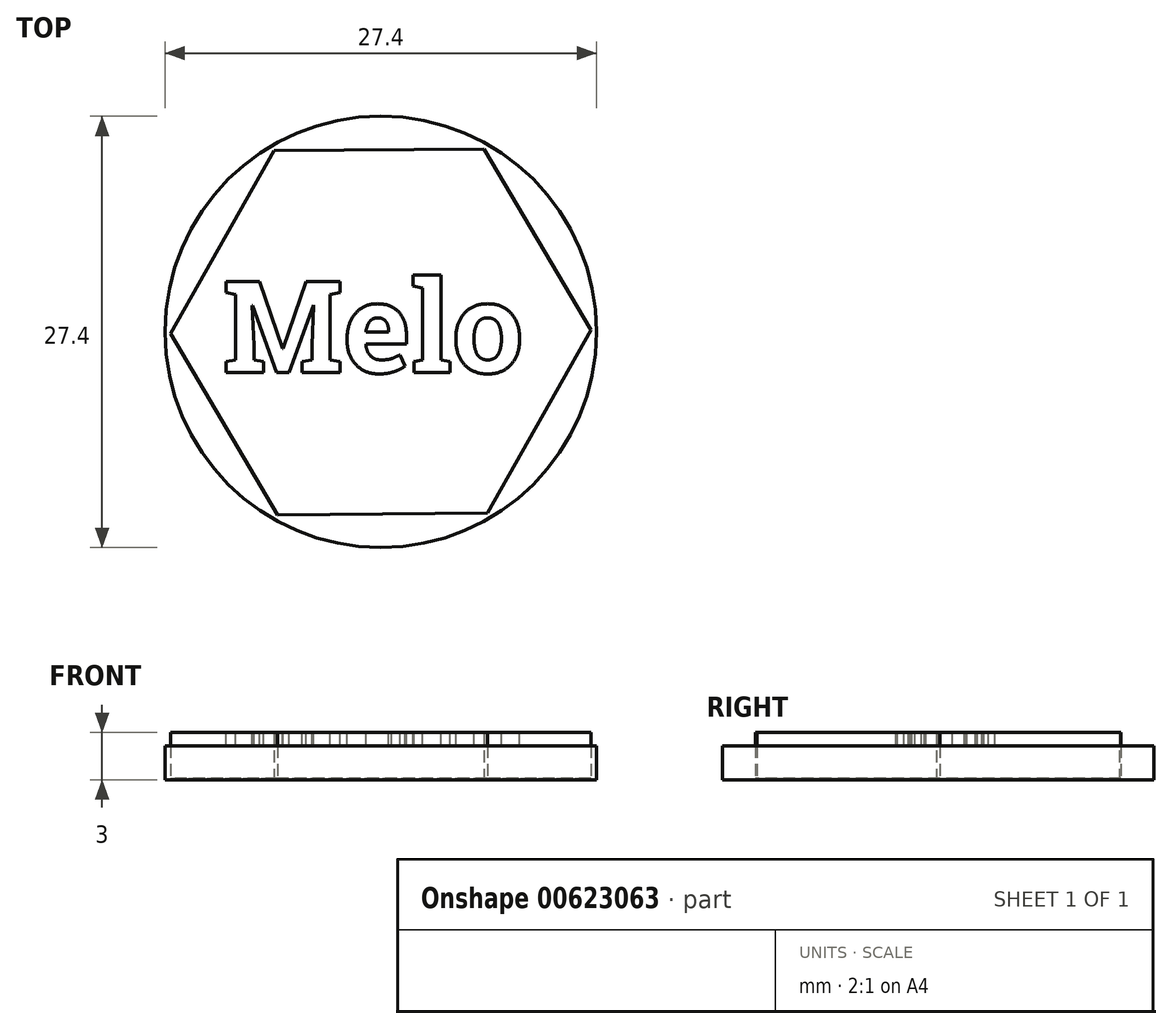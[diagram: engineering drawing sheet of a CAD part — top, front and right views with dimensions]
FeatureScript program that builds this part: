
annotation { "Feature Type Name" : "Feature", "Feature Type Description" : "" }
export const myFeature = defineFeature(function(context is Context, id is Id, definition is map)
    precondition{}
    {
        {
            var Q0;
            Q0=qCreatedBy(makeId("Top.planeOp"),FACE);
            var sketch = newSketch(context, id + "F0", { "sketchPlane" : qUnion([Q0])});
            skCircle(sketch, "E0", {"center": v(0, 0) * mm, "radius": 13.7 * mm});
            skSolve(sketch);
        }
        {
            var Q0;
            Q0=makeQuery(id+"F0.imprint","IMPRINT",FACE,{"disambiguationData":[TD([[makeQuery(id+"F0.imprint","IMPRINT",EDGE,{"derivedFrom":sQuery(id+"F0.wireOp",EDGE,"E0")}),1.0]])]});
            extrude(context, id + "F1", {"entities" : qUnion([Q0]), "depth" : 2.15 * mm, "offsetDistance" : 25 * mm});
        }
        {
            var Q0;
            Q0=makeQuery(id+"F0.imprint","IMPRINT",FACE,{"disambiguationData":[TD([[makeQuery(id+"F0.imprint","IMPRINT",EDGE,{"derivedFrom":sQuery(id+"F0.wireOp",EDGE,"E0")}),1.0]])]});
            var sketch = newSketch(context, id + "F2", { "sketchPlane" : qUnion([Q0])});
            skCircle(sketch, "E1.cCircle", {"center": v(0, 0) * mm, "radius": 11.56 * mm, "construction": true});
            skLineSegment(sketch, "E1.0", {"start": v(-13.35, -0.12) * mm, "end": v(-6.78, 11.5) * mm});
            skLineSegment(sketch, "E1.1", {"start": v(-6.78, 11.5) * mm, "end": v(6.57, 11.62) * mm});
            skLineSegment(sketch, "E1.2", {"start": v(6.57, 11.62) * mm, "end": v(13.35, 0.12) * mm});
            skLineSegment(sketch, "E1.3", {"start": v(13.35, 0.12) * mm, "end": v(6.78, -11.5) * mm});
            skLineSegment(sketch, "E1.4", {"start": v(6.78, -11.5) * mm, "end": v(-6.57, -11.62) * mm});
            skLineSegment(sketch, "E1.5", {"start": v(-6.57, -11.62) * mm, "end": v(-13.35, -0.12) * mm});
            skPoint(sketch, "E1.0.midPoint", {"position": v(-10.06, 5.69) * mm});
            skSolve(sketch);
        }
        {
            var Q0;
            Q0 = qSketchRegion(id + "F2", true);
            extrude(context, id + "F3", {"entities" : qUnion([Q0]), "depth" : 0.1 * mm, "offsetDistance" : 25 * mm});
        }
        {
            var Q0;
            Q0 = qSketchRegion(id + "F2", true);
            extrude(context, id + "F4", {"entities" : qUnion([Q0]), "depth" : 3 * mm, "offsetDistance" : 25 * mm});
        }
        {
            var Q0;
            Q0=makeQuery(id+"F4.opExtrude","CAP_FACE",FACE,{"disambiguationData":[OSD([sQuery(id+"F2.wireOp",EDGE,"E1.0"),sQuery(id+"F2.wireOp",EDGE,"E1.1"),sQuery(id+"F2.wireOp",EDGE,"E1.2"),sQuery(id+"F2.wireOp",EDGE,"E1.3"),sQuery(id+"F2.wireOp",EDGE,"E1.4"),sQuery(id+"F2.wireOp",EDGE,"E1.5")])],"isStart":false});
            var sketch = newSketch(context, id + "F5", { "sketchPlane" : qUnion([Q0])});
            skText(sketch, "E2", { "text": "Melo", "fontName": "RobotoSlab-Bold.ttf"});
            skPoint(sketch, "E2.secondSnap0", {"position": v(-10.06, 5.69) * mm});
            const initialGuessF5  = {"E2": [-0.01006, -0.00259, 1, 0, 0.00585]};
            skSetInitialGuess(sketch, initialGuessF5);
            skSolve(sketch);
        }
        {
            var Q0;
            Q0 = qSketchRegion(id + "F5", true);
            extrude(context, id + "F6", {"entities" : qUnion([Q0]), "operationType" : NewBodyOperationType.REMOVE, "endBound" : BoundingType.UP_TO_NEXT, "oppositeDirection" : true, "depth" : 2 * mm, "offsetDistance" : 25 * mm});
        }
    });
